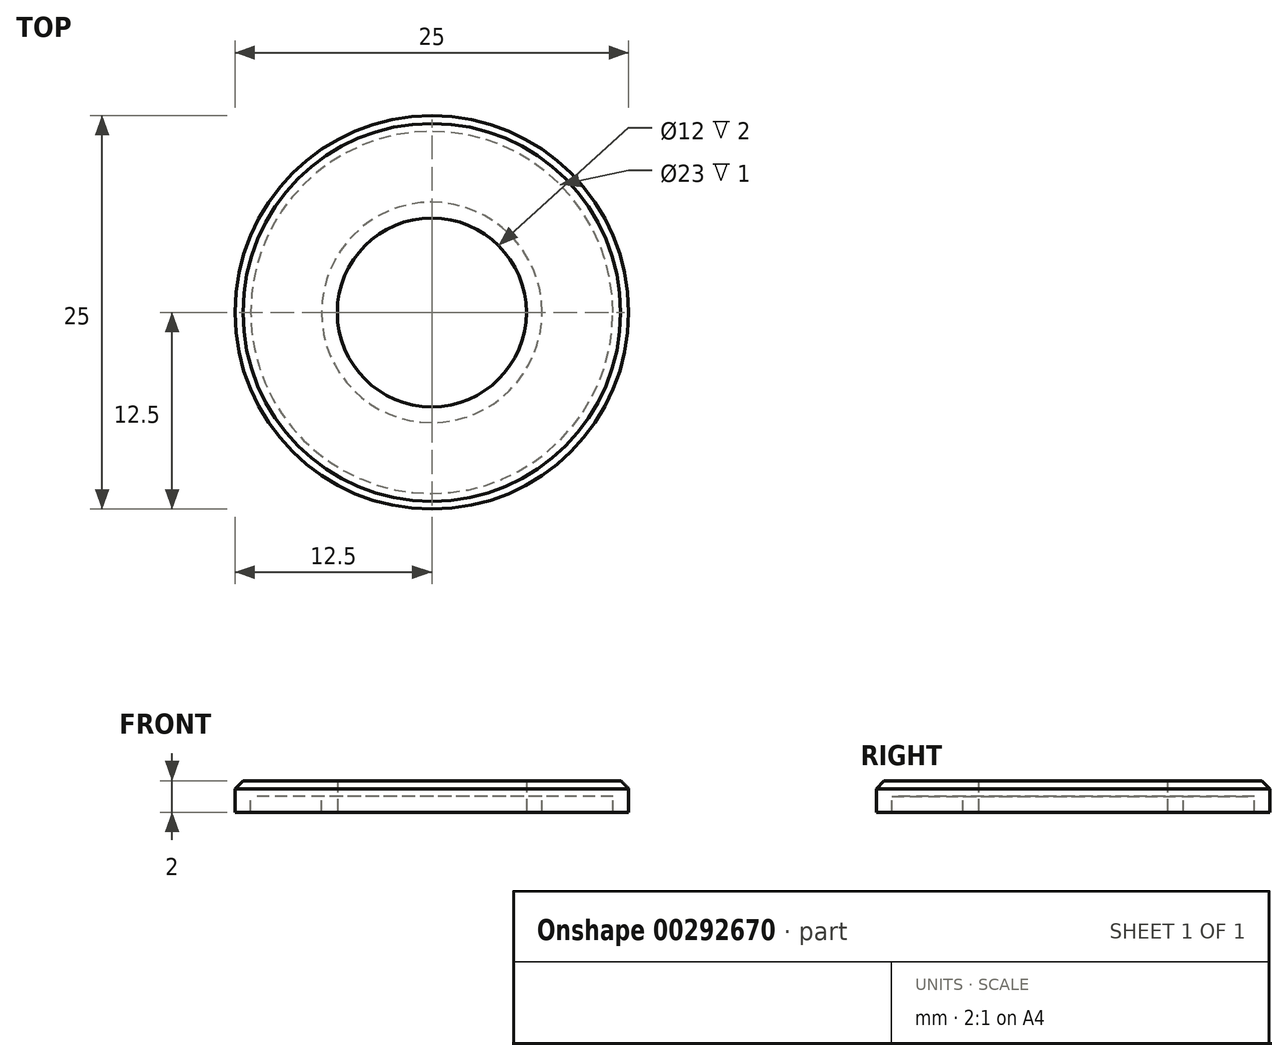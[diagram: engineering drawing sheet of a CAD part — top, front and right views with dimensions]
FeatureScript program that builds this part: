
annotation { "Feature Type Name" : "Feature", "Feature Type Description" : "" }
export const myFeature = defineFeature(function(context is Context, id is Id, definition is map)
    precondition{}
    {
        {
            var Q0;
            Q0=qCreatedBy(makeId("Top.planeOp"),FACE);
            var sketch = newSketch(context, id + "F0", { "sketchPlane" : qUnion([Q0])});
            skCircle(sketch, "E0", {"center": v(0, 0) * mm, "radius": 6 * mm});
            skCircle(sketch, "E1", {"center": v(0, 0) * mm, "radius": 12.5 * mm});
            skCircle(sketch, "E2", {"center": v(0, 0) * mm, "radius": 11.5 * mm});
            skCircle(sketch, "E3", {"center": v(0, 0) * mm, "radius": 7 * mm});
            skSolve(sketch);
        }
        {
            var Q0;
            Q0=makeQuery(id+"F0.imprint","IMPRINT",FACE,{"disambiguationData":[TD([[makeQuery(id+"F0.imprint","IMPRINT",EDGE,{"derivedFrom":sQuery(id+"F0.wireOp",EDGE,"E1")}),1.0]])]});
            var Q1;
            Q1=makeQuery(id+"F0.imprint","IMPRINT",FACE,{"disambiguationData":[TD([[makeQuery(id+"F0.imprint","IMPRINT",EDGE,{"derivedFrom":sQuery(id+"F0.wireOp",EDGE,"E2")}),1.0]])]});
            var Q2;
            Q2=makeQuery(id+"F0.imprint","IMPRINT",FACE,{"disambiguationData":[TD([[makeQuery(id+"F0.imprint","IMPRINT",EDGE,{"derivedFrom":sQuery(id+"F0.wireOp",EDGE,"E0")}),-1.0]])]});
            extrude(context, id + "F1", {"entities" : qUnion([Q0, Q1, Q2]), "depth" : 1 * mm, "offsetDistance" : 25 * mm});
        }
        {
            var Q0;
            Q0=makeQuery(id+"F0.imprint","IMPRINT",FACE,{"disambiguationData":[TD([[makeQuery(id+"F0.imprint","IMPRINT",EDGE,{"derivedFrom":sQuery(id+"F0.wireOp",EDGE,"E1")}),1.0]])]});
            var Q1;
            Q1=makeQuery(id+"F0.imprint","IMPRINT",FACE,{"disambiguationData":[TD([[makeQuery(id+"F0.imprint","IMPRINT",EDGE,{"derivedFrom":sQuery(id+"F0.wireOp",EDGE,"E0")}),-1.0]])]});
            extrude(context, id + "F2", {"entities" : qUnion([Q0, Q1]), "operationType" : NewBodyOperationType.ADD, "oppositeDirection" : true, "depth" : 1 * mm, "offsetDistance" : 25 * mm});
        }
        {
            var Q0;
            Q0=makeQuery(id+"F1.opExtrude","CAP_EDGE",EDGE,{"disambiguationData":[OSD([sQuery(id+"F0.wireOp",EDGE,"E1")])],"isStart":false});
            chamfer(context, id + "F3", {"entities" : qUnion([Q0]), "width" : 0.5 * mm, "tangentPropagation" : true});
        }
    });
